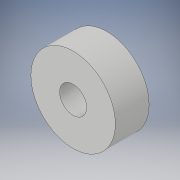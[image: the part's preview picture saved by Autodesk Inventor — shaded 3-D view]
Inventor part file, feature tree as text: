
AUTODESK INVENTOR PART (.ipt)
format: ipt  version: 2017 (Build 210142000, 142)  size: 96,256 bytes
history: native  units: in
note: dims shown in document units (in); Inventor stores cm internally (conversion verified against a paired STEP export)
features: extrude x1, sketch x1
ambient origin geometry x8: Origin, YZ Plane, XZ Plane, XY Plane, X Axis, Y Axis, Z Axis, Center Point
bodies: Solid1 (feature_tree)
feature tree (2):
  extrude  "Extrusion1"  Depth=0.3937in
  sketch  "Sketch1"  dims[d0=0.9843in d1=0.315in d2=0.3937in d3=0.0in]
